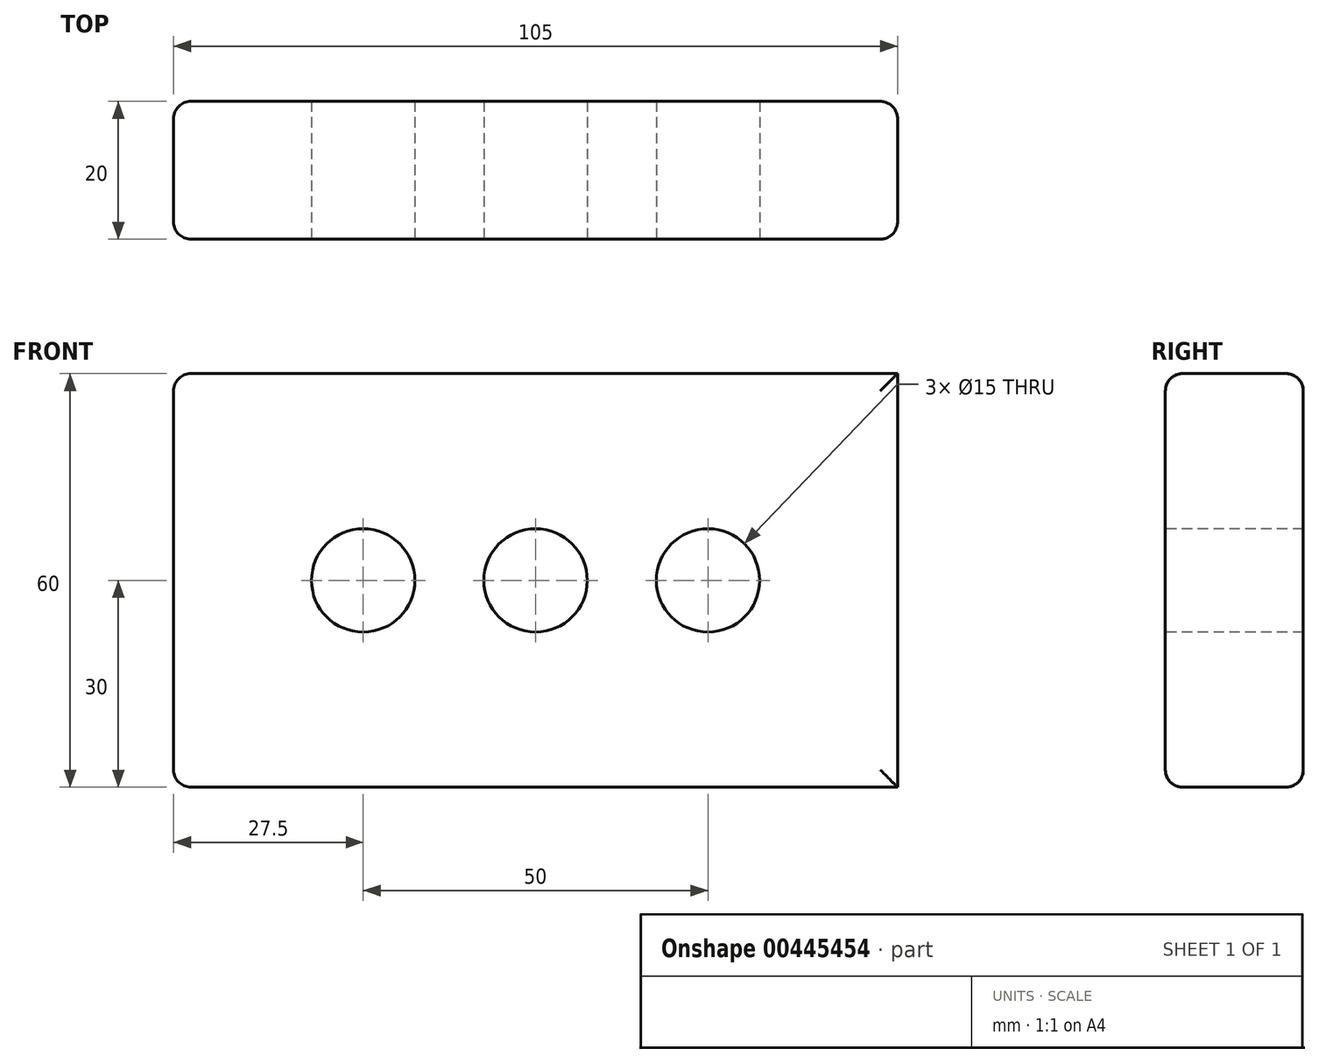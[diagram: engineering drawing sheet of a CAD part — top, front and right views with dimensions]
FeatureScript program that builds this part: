
annotation { "Feature Type Name" : "Feature", "Feature Type Description" : "" }
export const myFeature = defineFeature(function(context is Context, id is Id, definition is map)
    precondition{}
    {
        {
            var Q0;
            Q0=qCreatedBy(makeId("Front.planeOp"),FACE);
            var sketch = newSketch(context, id + "F0", { "sketchPlane" : qUnion([Q0])});
            skLineSegment(sketch, "E0.bottom", {"start": v(52.5, 30) * mm, "end": v(-52.5, 30) * mm});
            skLineSegment(sketch, "E0.top", {"start": v(52.5, -30) * mm, "end": v(-52.5, -30) * mm});
            skLineSegment(sketch, "E0.left", {"start": v(52.5, 30) * mm, "end": v(52.5, -30) * mm});
            skLineSegment(sketch, "E0.right", {"start": v(-52.5, 30) * mm, "end": v(-52.5, -30) * mm});
            skPoint(sketch, "E0.middle", {"position": v(0, 0) * mm});
            skSolve(sketch);
        }
        {
            var Q0;
            Q0 = qSketchRegion(id + "F0", true);
            var Q1;
            Q1=makeQuery(id+"F0.imprint","IMPRINT",FACE,{"disambiguationData":[TD([[makeQuery(id+"F0.imprint","IMPRINT",EDGE,{"derivedFrom":sQuery(id+"F0.wireOp",EDGE,"E0.bottom")}),1.0]])]});
            extrude(context, id + "F1", {"entities" : qUnion([Q0, Q1]), "depth" : 20 * mm});
        }
        {
            var Q0;
            Q0=makeQuery(id+"F1.opExtrude","CAP_FACE",FACE,{"disambiguationData":[OSD([sQuery(id+"F0.wireOp",EDGE,"E0.bottom"),sQuery(id+"F0.wireOp",EDGE,"E0.top"),sQuery(id+"F0.wireOp",EDGE,"E0.left"),sQuery(id+"F0.wireOp",EDGE,"E0.right")])],"isStart":false});
            var sketch = newSketch(context, id + "F2", { "sketchPlane" : qUnion([Q0])});
            skCircle(sketch, "E1", {"center": v(0, 0) * mm, "radius": 7.5 * mm});
            skCircle(sketch, "E2", {"center": v(-25, 0) * mm, "radius": 7.5 * mm});
            skCircle(sketch, "E3", {"center": v(25, 0) * mm, "radius": 7.5 * mm});
            skSolve(sketch);
        }
        {
            var Q0;
            Q0=makeQuery(id+"F2.imprint","IMPRINT",FACE,{"disambiguationData":[TD([[makeQuery(id+"F2.imprint","IMPRINT",EDGE,{"derivedFrom":sQuery(id+"F2.wireOp",EDGE,"E2")}),1.0]])]});
            var Q1;
            Q1=makeQuery(id+"F2.imprint","IMPRINT",FACE,{"disambiguationData":[TD([[makeQuery(id+"F2.imprint","IMPRINT",EDGE,{"derivedFrom":sQuery(id+"F2.wireOp",EDGE,"E1")}),1.0]])]});
            var Q2;
            Q2=makeQuery(id+"F2.imprint","IMPRINT",FACE,{"disambiguationData":[TD([[makeQuery(id+"F2.imprint","IMPRINT",EDGE,{"derivedFrom":sQuery(id+"F2.wireOp",EDGE,"E3")}),1.0]])]});
            extrude(context, id + "F3", {"entities" : qUnion([Q0, Q1, Q2]), "operationType" : NewBodyOperationType.REMOVE, "oppositeDirection" : true, "depth" : 25 * mm});
        }
        {
            var Q0;
            Q0=makeQuery(id+"F1.opExtrude","CAP_EDGE",EDGE,{"disambiguationData":[OSD([sQuery(id+"F0.wireOp",EDGE,"E0.bottom")])],"isStart":false});
            var Q1;
            Q1=makeQuery(id+"F1.opExtrude","CAP_EDGE",EDGE,{"disambiguationData":[OSD([sQuery(id+"F0.wireOp",EDGE,"E0.right")])],"isStart":false});
            var Q2;
            Q2=makeQuery(id+"F1.opExtrude","CAP_EDGE",EDGE,{"disambiguationData":[OSD([sQuery(id+"F0.wireOp",EDGE,"E0.top")])],"isStart":false});
            var Q3;
            Q3=makeQuery(id+"F1.opExtrude","CAP_EDGE",EDGE,{"disambiguationData":[OSD([sQuery(id+"F0.wireOp",EDGE,"E0.left")])],"isStart":false});
            var Q4;
            Q4=makeQuery(id+"F1.opExtrude","CAP_EDGE",EDGE,{"disambiguationData":[OSD([sQuery(id+"F0.wireOp",EDGE,"E0.top")])],"isStart":true});
            var Q5;
            Q5=makeQuery(id+"F1.opExtrude","CAP_EDGE",EDGE,{"disambiguationData":[OSD([sQuery(id+"F0.wireOp",EDGE,"E0.bottom")])],"isStart":true});
            var Q6;
            Q6=makeQuery(id+"F1.opExtrude","CAP_EDGE",EDGE,{"disambiguationData":[OSD([sQuery(id+"F0.wireOp",EDGE,"E0.left")])],"isStart":true});
            fillet(context, id + "F4", {"entities" : qUnion([Q0, Q1, Q2, Q3, Q4, Q5, Q6]), "radius" : 2.5 * mm, "tangentPropagation" : true, "allowEdgeOverflow" : false});
        }
        {
            var Q0;
            Q0=makeQuery(id+"F1.opExtrude","CAP_EDGE",EDGE,{"disambiguationData":[OSD([sQuery(id+"F0.wireOp",EDGE,"E0.right")])],"isStart":true});
            fillet(context, id + "F5", {"entities" : qUnion([Q0]), "radius" : 2.5 * mm, "tangentPropagation" : true, "allowEdgeOverflow" : false});
        }
    });
